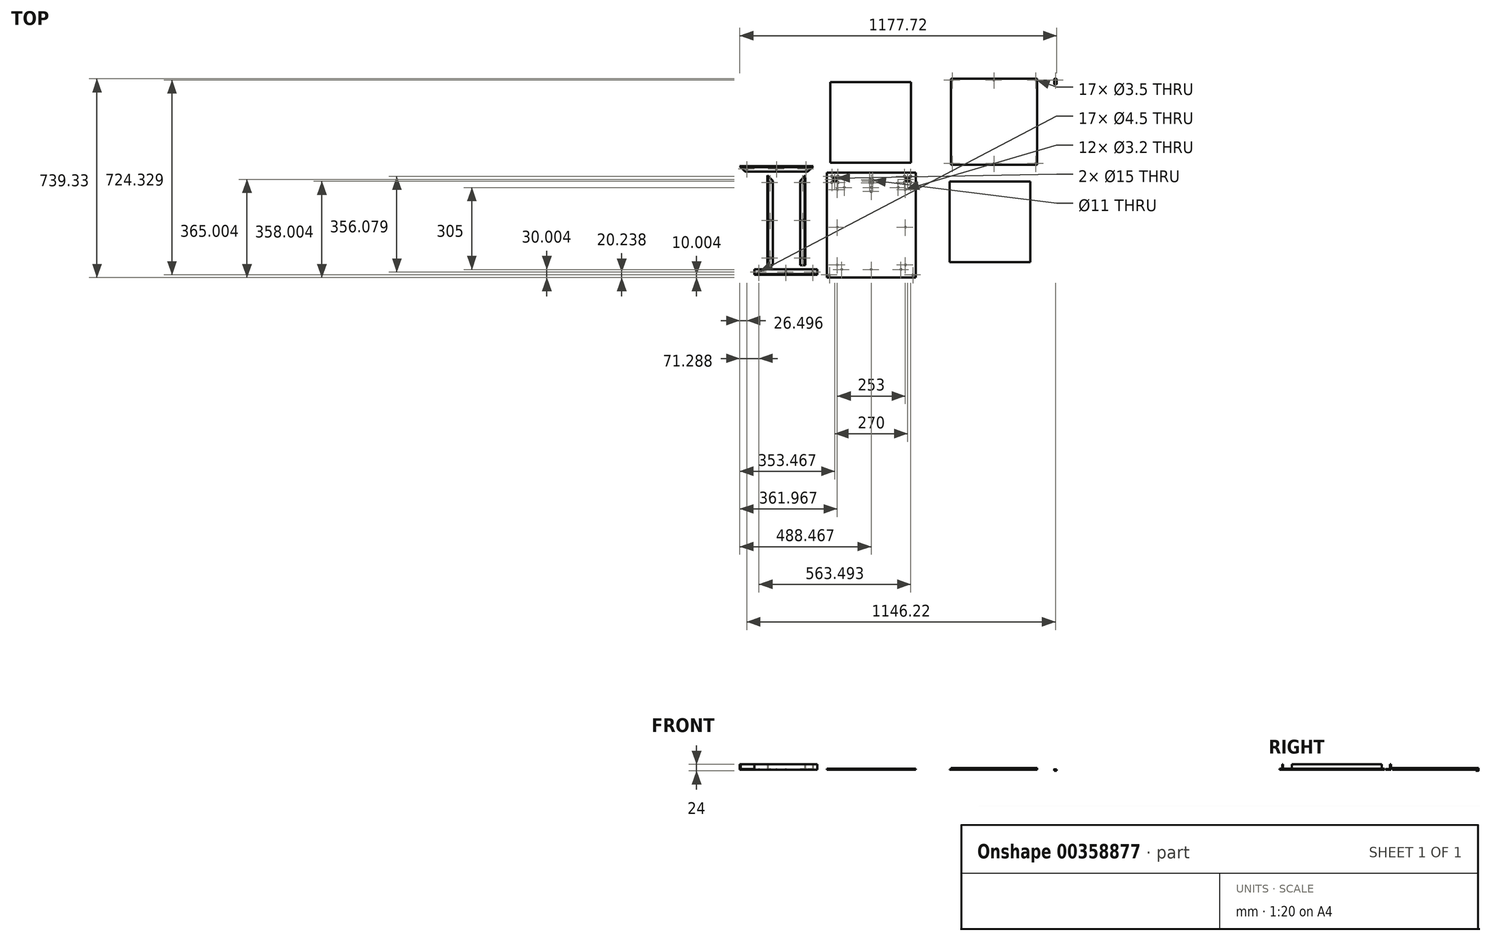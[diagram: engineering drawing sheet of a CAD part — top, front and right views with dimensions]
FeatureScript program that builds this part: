
annotation { "Feature Type Name" : "Feature", "Feature Type Description" : "" }
export const myFeature = defineFeature(function(context is Context, id is Id, definition is map)
    precondition{}
    {
        {
            var Q0;
            Q0=qCreatedBy(makeId("Top.planeOp"),FACE);
            var sketch = newSketch(context, id + "F0", { "sketchPlane" : qUnion([Q0])});
            skLineSegment(sketch, "E0.bottom", {"start": v(150, 187.33) * mm, "end": v(480, 187.33) * mm});
            skLineSegment(sketch, "E0.top", {"start": v(150, -202.67) * mm, "end": v(480, -202.67) * mm});
            skLineSegment(sketch, "E0.left", {"start": v(150, 187.33) * mm, "end": v(150, -202.67) * mm});
            skLineSegment(sketch, "E0.right", {"start": v(480, 187.33) * mm, "end": v(480, -202.67) * mm});
            skCircle(sketch, "E1", {"center": v(180, 162.33) * mm, "radius": 7.5 * mm});
            skCircle(sketch, "E2", {"center": v(450, 162.33) * mm, "radius": 7.5 * mm});
            skCircle(sketch, "E3", {"center": v(315, 155.33) * mm, "radius": 5.5 * mm});
            skPoint(sketch, "E3.centerSnap0", {"position": v(315, 187.33) * mm});
            skLineSegment(sketch, "E4", {"start": v(150, -202.67) * mm, "end": v(480, 187.33) * mm, "construction": true});
            skLineSegment(sketch, "E5.bottom", {"start": v(470, -192.67) * mm, "end": v(160, -192.67) * mm, "construction": true});
            skLineSegment(sketch, "E5.top", {"start": v(470, 117.33) * mm, "end": v(160, 117.33) * mm, "construction": true});
            skLineSegment(sketch, "E5.left", {"start": v(470, -192.67) * mm, "end": v(470, 117.33) * mm, "construction": true});
            skLineSegment(sketch, "E5.right", {"start": v(160, -192.67) * mm, "end": v(160, 117.33) * mm, "construction": true});
            skPoint(sketch, "E5.middle", {"position": v(315, -37.67) * mm});
            skCircle(sketch, "E6", {"center": v(315, 117.33) * mm, "radius": 1.75 * mm});
            skCircle(sketch, "E7", {"center": v(160, -192.67) * mm, "radius": 1.75 * mm});
            skCircle(sketch, "E8", {"center": v(470, -192.67) * mm, "radius": 1.75 * mm});
            skLineSegment(sketch, "E9", {"start": v(315, -7.67) * mm, "end": v(315, -37.67) * mm, "construction": true});
            skLineSegment(sketch, "E10", {"start": v(315, -37.67) * mm, "end": v(315, -37.67) * mm});
            skCircle(sketch, "E11", {"center": v(180, 162.33) * mm, "radius": 16 * mm, "construction": true});
            skCircle(sketch, "E12", {"center": v(168.7, 151.02) * mm, "radius": 2.25 * mm});
            skCircle(sketch, "E13", {"center": v(168.7, 173.65) * mm, "radius": 2.25 * mm});
            skCircle(sketch, "E14", {"center": v(191.32, 173.65) * mm, "radius": 2.25 * mm});
            skCircle(sketch, "E15", {"center": v(191.32, 151.02) * mm, "radius": 2.25 * mm});
            skLineSegment(sketch, "E16.bottom", {"start": v(168.7, 173.65) * mm, "end": v(191.32, 173.65) * mm, "construction": true});
            skLineSegment(sketch, "E16.top", {"start": v(168.7, 151.02) * mm, "end": v(191.32, 151.02) * mm, "construction": true});
            skLineSegment(sketch, "E16.left", {"start": v(168.7, 173.65) * mm, "end": v(168.7, 151.02) * mm, "construction": true});
            skLineSegment(sketch, "E16.right", {"start": v(191.32, 173.65) * mm, "end": v(191.32, 151.02) * mm, "construction": true});
            skCircle(sketch, "E17", {"center": v(450, 162.33) * mm, "radius": 16 * mm, "construction": true});
            skLineSegment(sketch, "E18.bottom", {"start": v(438.7, 173.65) * mm, "end": v(461.32, 173.65) * mm, "construction": true});
            skLineSegment(sketch, "E18.top", {"start": v(438.7, 151.02) * mm, "end": v(461.32, 151.02) * mm, "construction": true});
            skLineSegment(sketch, "E18.left", {"start": v(438.7, 173.65) * mm, "end": v(438.7, 151.02) * mm, "construction": true});
            skLineSegment(sketch, "E18.right", {"start": v(461.32, 173.65) * mm, "end": v(461.32, 151.02) * mm, "construction": true});
            skCircle(sketch, "E19", {"center": v(438.7, 173.65) * mm, "radius": 2.25 * mm});
            skCircle(sketch, "E20", {"center": v(461.32, 173.65) * mm, "radius": 2.25 * mm});
            skCircle(sketch, "E21", {"center": v(461.32, 151.02) * mm, "radius": 2.25 * mm});
            skCircle(sketch, "E22", {"center": v(438.7, 151.02) * mm, "radius": 2.25 * mm});
            skCircle(sketch, "E23", {"center": v(315, 155.33) * mm, "radius": 8 * mm, "construction": true});
            skLineSegment(sketch, "E24.bottom", {"start": v(309.35, 161) * mm, "end": v(320.66, 161) * mm, "construction": true});
            skLineSegment(sketch, "E24.top", {"start": v(309.35, 149.68) * mm, "end": v(320.66, 149.68) * mm, "construction": true});
            skLineSegment(sketch, "E24.left", {"start": v(309.35, 161) * mm, "end": v(309.35, 149.68) * mm, "construction": true});
            skLineSegment(sketch, "E24.right", {"start": v(320.66, 161) * mm, "end": v(320.66, 149.68) * mm, "construction": true});
            skCircle(sketch, "E25", {"center": v(309.35, 161) * mm, "radius": 1.75 * mm});
            skCircle(sketch, "E26", {"center": v(320.66, 161) * mm, "radius": 1.75 * mm});
            skCircle(sketch, "E27", {"center": v(320.66, 149.68) * mm, "radius": 1.75 * mm});
            skCircle(sketch, "E28", {"center": v(309.35, 149.68) * mm, "radius": 1.75 * mm});
            skCircle(sketch, "E29", {"center": v(188.5, -155.42) * mm, "radius": 1.6 * mm});
            skCircle(sketch, "E30", {"center": v(315, -172.67) * mm, "radius": 1.6 * mm});
            skPoint(sketch, "E30.centerSnap0", {"position": v(315, -202.67) * mm});
            skCircle(sketch, "E31", {"center": v(205, -172.67) * mm, "radius": 1.6 * mm});
            skCircle(sketch, "E32", {"center": v(425, -172.67) * mm, "radius": 1.6 * mm});
            skCircle(sketch, "E33", {"center": v(441.5, -155.42) * mm, "radius": 1.6 * mm});
            skCircle(sketch, "E34", {"center": v(188.5, -15.42) * mm, "radius": 1.6 * mm});
            skCircle(sketch, "E35", {"center": v(188.5, 124.58) * mm, "radius": 1.6 * mm});
            skCircle(sketch, "E36", {"center": v(441.5, -15.42) * mm, "radius": 1.6 * mm});
            skCircle(sketch, "E37", {"center": v(441.5, 124.58) * mm, "radius": 1.6 * mm});
            skCircle(sketch, "E38", {"center": v(315, 132.33) * mm, "radius": 1.6 * mm});
            skCircle(sketch, "E39", {"center": v(415, 132.33) * mm, "radius": 1.6 * mm});
            skCircle(sketch, "E40", {"center": v(215, 132.33) * mm, "radius": 1.6 * mm});
            skSolve(sketch);
        }
        {
            var Q0;
            Q0=makeQuery(id+"F0.imprint","IMPRINT",FACE,{"disambiguationData":[TD([[makeQuery(id+"F0.imprint","IMPRINT",EDGE,{"derivedFrom":sQuery(id+"F0.wireOp",EDGE,"E0.bottom")}),-1.0]])]});
            extrude(context, id + "F1", {"entities" : qUnion([Q0]), "depth" : 4 * mm});
        }
        {
            var Q0;
            Q0=qCreatedBy(makeId("Top.planeOp"),FACE);
            var sketch = newSketch(context, id + "F2", { "sketchPlane" : qUnion([Q0])});
            skLineSegment(sketch, "E41.bottom", {"start": v(605.69, 155) * mm, "end": v(905.69, 155) * mm});
            skLineSegment(sketch, "E41.top", {"start": v(605.69, -145) * mm, "end": v(905.69, -145) * mm});
            skLineSegment(sketch, "E41.left", {"start": v(605.69, 155) * mm, "end": v(605.69, -145) * mm});
            skLineSegment(sketch, "E41.right", {"start": v(905.69, 155) * mm, "end": v(905.69, -145) * mm});
            skSolve(sketch);
        }
        {
            var Q0;
            Q0=makeQuery(id+"F2.imprint","IMPRINT",FACE,{"disambiguationData":[TD([[makeQuery(id+"F2.imprint","IMPRINT",EDGE,{"derivedFrom":sQuery(id+"F2.wireOp",EDGE,"E41.bottom")}),-1.0]])]});
            extrude(context, id + "F3", {"entities" : qUnion([Q0]), "depth" : 2 * mm});
        }
        {
            var Q0;
            Q0=qCreatedBy(makeId("Top.planeOp"),FACE);
            var sketch = newSketch(context, id + "F4", { "sketchPlane" : qUnion([Q0])});
            skLineSegment(sketch, "E42.bottom", {"start": v(611.16, 536.66) * mm, "end": v(931.16, 536.66) * mm});
            skLineSegment(sketch, "E42.top", {"start": v(611.16, 216.66) * mm, "end": v(931.16, 216.66) * mm});
            skLineSegment(sketch, "E42.left", {"start": v(611.16, 536.66) * mm, "end": v(611.16, 216.66) * mm});
            skLineSegment(sketch, "E42.right", {"start": v(931.16, 536.66) * mm, "end": v(931.16, 216.66) * mm});
            skCircle(sketch, "E43", {"center": v(771.16, 531.66) * mm, "radius": 1.75 * mm});
            skPoint(sketch, "E43.centerSnap0", {"position": v(771.16, 536.66) * mm});
            skLineSegment(sketch, "E44", {"start": v(611.16, 216.66) * mm, "end": v(931.16, 536.66) * mm, "construction": true});
            skLineSegment(sketch, "E45", {"start": v(611.16, 536.66) * mm, "end": v(931.16, 216.66) * mm, "construction": true});
            skCircle(sketch, "E46", {"center": v(616.16, 221.66) * mm, "radius": 1.75 * mm});
            skCircle(sketch, "E47", {"center": v(926.16, 221.66) * mm, "radius": 1.75 * mm});
            skCircle(sketch, "E48", {"center": v(771.16, 221.66) * mm, "radius": 1.75 * mm});
            skPoint(sketch, "E48.centerSnap0", {"position": v(771.16, 216.66) * mm});
            skCircle(sketch, "E49", {"center": v(616.16, 531.66) * mm, "radius": 1.75 * mm});
            skCircle(sketch, "E50", {"center": v(926.16, 531.66) * mm, "radius": 1.75 * mm});
            skSolve(sketch);
        }
        {
            var Q0;
            Q0=makeQuery(id+"F4.imprint","IMPRINT",FACE,{"disambiguationData":[TD([[makeQuery(id+"F4.imprint","IMPRINT",EDGE,{"derivedFrom":sQuery(id+"F4.wireOp",EDGE,"E42.bottom")}),-1.0]])]});
            extrude(context, id + "F5", {"entities" : qUnion([Q0]), "depth" : 6 * mm});
        }
        {
            var Q0;
            Q0=qCreatedBy(makeId("Top.planeOp"),FACE);
            var sketch = newSketch(context, id + "F6", { "sketchPlane" : qUnion([Q0])});
            skLineSegment(sketch, "E51.bottom", {"start": v(162.3, 524.65) * mm, "end": v(462.3, 524.65) * mm});
            skLineSegment(sketch, "E51.top", {"start": v(162.3, 224.65) * mm, "end": v(462.3, 224.65) * mm});
            skLineSegment(sketch, "E51.left", {"start": v(162.3, 524.65) * mm, "end": v(162.3, 224.65) * mm});
            skLineSegment(sketch, "E51.right", {"start": v(462.3, 524.65) * mm, "end": v(462.3, 224.65) * mm});
            skSolve(sketch);
        }
        {
            var Q0;
            Q0=qSketchRegion(id+"F6",true);
            extrude(context, id + "F7", {"entities" : qUnion([Q0]), "depth" : 4 * mm});
        }
        {
            var Q0;
            Q0=qCreatedBy(makeId("Top.planeOp"),FACE);
            var sketch = newSketch(context, id + "F8", { "sketchPlane" : qUnion([Q0])});
            skCircle(sketch, "E52", {"center": v(999.26, 531.22) * mm, "radius": 1.75 * mm});
            skCircle(sketch, "E53", {"center": v(999.26, 531.22) * mm, "radius": 5 * mm});
            skLineSegment(sketch, "E54.bottom", {"start": v(994.26, 536.22) * mm, "end": v(1004.26, 536.22) * mm});
            skLineSegment(sketch, "E54.top", {"start": v(994.26, 516.22) * mm, "end": v(1004.26, 516.22) * mm});
            skLineSegment(sketch, "E54.left", {"start": v(994.26, 536.22) * mm, "end": v(994.26, 516.22) * mm});
            skLineSegment(sketch, "E54.right", {"start": v(1004.26, 536.22) * mm, "end": v(1004.26, 516.22) * mm});
            skSolve(sketch);
        }
        {
            var Q0;
            Q0=makeQuery(id+"F8.imprint","IMPRINT",FACE,{"disambiguationData":[TD([[makeQuery(id+"F8.imprint","IMPRINT",EDGE,{"derivedFrom":sQuery(id+"F8.wireOp",EDGE,"E52")}),-1.0]])]});
            var Q1;
            {var subQ0=sQuery(id+"F8.wireOp",EDGE,"E54.bottom");var subQ1=sQuery(id+"F8.wireOp",EDGE,"E53");var subQ2=makeQuery(id+"F8.imprint","INTERSECT",VERTEX,{"derivedFrom":[subQ1,subQ0]});Q1=makeQuery(id+"F8.imprint","IMPRINT",FACE,{"disambiguationData":[TD([[makeQuery(id+"F8.imprint","IMPRINT",EDGE,{"disambiguationData":[TD([[subQ2,-1.0]])],"derivedFrom":subQ1}),-1.0]])]});}
            var Q2;
            {var subQ0=sQuery(id+"F8.wireOp",EDGE,"E54.bottom");var subQ1=sQuery(id+"F8.wireOp",EDGE,"E53");var subQ2=makeQuery(id+"F8.imprint","INTERSECT",VERTEX,{"derivedFrom":[subQ1,subQ0]});Q2=makeQuery(id+"F8.imprint","IMPRINT",FACE,{"disambiguationData":[TD([[makeQuery(id+"F8.imprint","IMPRINT",EDGE,{"disambiguationData":[TD([[subQ2,1.0]])],"derivedFrom":subQ1}),-1.0]])]});}
            extrude(context, id + "F9", {"entities" : qUnion([Q0, Q1, Q2]), "oppositeDirection" : true, "depth" : 4 * mm});
        }
        {
            var Q0;
            Q0=qSketchRegion(id+"F8",true);
            extrude(context, id + "F10", {"entities" : qUnion([Q0]), "operationType" : NewBodyOperationType.ADD, "depth" : 2 * mm});
        }
        {
            var Q0;
            Q0=makeQuery(id+"F10.opExtrude","SWEPT_EDGE",EDGE,{"disambiguationData":[OSD([sQuery(id+"F8.wireOp",EDGE,"E54.top"),sQuery(id+"F8.wireOp",EDGE,"E54.left")])]});
            var Q1;
            Q1=makeQuery(id+"F10.opExtrude","SWEPT_EDGE",EDGE,{"disambiguationData":[OSD([sQuery(id+"F8.wireOp",EDGE,"E54.top"),sQuery(id+"F8.wireOp",EDGE,"E54.right")])]});
            var Q2;
            {var subQ0=sQuery(id+"F8.wireOp",EDGE,"E54.right");var subQ1=sQuery(id+"F8.wireOp",EDGE,"E54.bottom");Q2=makeQuery(id+"F10.boolean.opBoolean","MERGE",EDGE,{"derivedFrom":[makeQuery(id+"F9.opExtrude","SWEPT_EDGE",EDGE,{"disambiguationData":[OSD([subQ1,subQ0])]}),makeQuery(id+"F10.opExtrude","SWEPT_EDGE",EDGE,{"disambiguationData":[OSD([subQ1,subQ0])]})]});}
            var Q3;
            {var subQ0=sQuery(id+"F8.wireOp",EDGE,"E54.left");var subQ1=sQuery(id+"F8.wireOp",EDGE,"E54.bottom");Q3=makeQuery(id+"F10.boolean.opBoolean","MERGE",EDGE,{"derivedFrom":[makeQuery(id+"F9.opExtrude","SWEPT_EDGE",EDGE,{"disambiguationData":[OSD([subQ1,subQ0])]}),makeQuery(id+"F10.opExtrude","SWEPT_EDGE",EDGE,{"disambiguationData":[OSD([subQ1,subQ0])]})]});}
            fillet(context, id + "F11", {"entities" : qUnion([Q0, Q1, Q2, Q3]), "radius" : 2 * mm, "tangentPropagation" : true, "allowEdgeOverflow" : false});
        }
        {
            var Q0;
            Q0=qCreatedBy(makeId("Top.planeOp"),FACE);
            var sketch = newSketch(context, id + "F12", { "sketchPlane" : qUnion([Q0])});
            skLineSegment(sketch, "E55.bottom", {"start": v(-70.66, 177.44) * mm, "end": v(-50.66, 177.44) * mm});
            skLineSegment(sketch, "E55.top", {"start": v(-70.66, -157.06) * mm, "end": v(-50.66, -157.06) * mm});
            skLineSegment(sketch, "E55.left", {"start": v(-70.66, 177.44) * mm, "end": v(-70.66, -157.06) * mm});
            skLineSegment(sketch, "E55.right", {"start": v(-50.66, 177.44) * mm, "end": v(-50.66, -157.06) * mm});
            skLineSegment(sketch, "E56", {"start": v(-70.66, 177.44) * mm, "end": v(-50.66, 157.44) * mm});
            skCircle(sketch, "E57", {"center": v(-60.66, -129.8) * mm, "radius": 2.25 * mm});
            skPoint(sketch, "E57.centerSnap0", {"position": v(-60.66, -157.06) * mm});
            skCircle(sketch, "E58", {"center": v(-60.66, 10.2) * mm, "radius": 2.25 * mm});
            skPoint(sketch, "E58.centerSnap0", {"position": v(-50.66, 10.2) * mm});
            skCircle(sketch, "E59", {"center": v(-60.66, 150.2) * mm, "radius": 2.25 * mm});
            skPoint(sketch, "E59.centerSnap0", {"position": v(-60.66, 167.44) * mm});
            skSolve(sketch);
        }
        {
            var Q0;
            {var subQ0=sQuery(id+"F12.wireOp",EDGE,"E55.top");Q0=makeQuery(id+"F12.imprint","IMPRINT",FACE,{"disambiguationData":[TD([[makeQuery(id+"F12.imprint","IMPRINT",EDGE,{"derivedFrom":subQ0}),1.0]])]});}
            extrude(context, id + "F13", {"entities" : qUnion([Q0]), "depth" : 3 * mm});
        }
        {
            var Q0;
            Q0=makeQuery(id+"F13.opExtrude","CAP_FACE",FACE,{"disambiguationData":[OSD([sQuery(id+"F12.wireOp",EDGE,"E55.top"),sQuery(id+"F12.wireOp",EDGE,"E55.left"),sQuery(id+"F12.wireOp",EDGE,"E55.right"),sQuery(id+"F12.wireOp",EDGE,"E56")])],"isStart":true});
            var sketch = newSketch(context, id + "F14", { "sketchPlane" : qUnion([Q0])});
            skLineSegment(sketch, "E60", {"start": v(-70.66, -177.44) * mm, "end": v(-70.66, 157.06) * mm});
            skLineSegment(sketch, "E61", {"start": v(-70.66, 157.06) * mm, "end": v(-67.66, 157.06) * mm});
            skLineSegment(sketch, "E62", {"start": v(-67.66, 157.06) * mm, "end": v(-67.66, -174.44) * mm});
            skLineSegment(sketch, "E63", {"start": v(-67.66, -174.44) * mm, "end": v(-70.66, -177.44) * mm});
            skSolve(sketch);
        }
        {
            var Q0;
            Q0=makeQuery(id+"F14.imprint","IMPRINT",FACE,{"disambiguationData":[TD([[makeQuery(id+"F14.imprint","IMPRINT",EDGE,{"derivedFrom":sQuery(id+"F14.wireOp",EDGE,"E60")}),-1.0]])]});
            extrude(context, id + "F15", {"entities" : qUnion([Q0]), "operationType" : NewBodyOperationType.ADD, "oppositeDirection" : true, "depth" : 20 * mm});
        }
        {
            var Q0;
            Q0=makeQuery(id+"F13.opExtrude","SWEPT_BODY",BODY,{"disambiguationData":[OSD([sQuery(id+"F12.wireOp",EDGE,"E55.top"),sQuery(id+"F12.wireOp",EDGE,"E55.left"),sQuery(id+"F12.wireOp",EDGE,"E55.right"),sQuery(id+"F12.wireOp",EDGE,"E56"),sQuery(id+"F12.wireOp",EDGE,"E57"),sQuery(id+"F12.wireOp",EDGE,"E58"),sQuery(id+"F12.wireOp",EDGE,"E59")])]});
            var Q1;
            Q1=qCreatedBy(makeId("Right.planeOp"),FACE);
            mirror(context, id + "F16", {"entities" : qUnion([Q0]), "mirrorPlane" : qUnion([Q1])});
        }
        {
            var Q0;
            Q0=qCreatedBy(makeId("Top.planeOp"),FACE);
            var sketch = newSketch(context, id + "F17", { "sketchPlane" : qUnion([Q0])});
            skLineSegment(sketch, "E64.bottom", {"start": v(-173.46, 211.15) * mm, "end": v(99.54, 211.15) * mm});
            skLineSegment(sketch, "E64.top", {"start": v(-173.46, 191.15) * mm, "end": v(99.54, 191.15) * mm});
            skLineSegment(sketch, "E64.left", {"start": v(-173.46, 211.15) * mm, "end": v(-173.46, 191.15) * mm});
            skLineSegment(sketch, "E64.right", {"start": v(99.54, 211.15) * mm, "end": v(99.54, 191.15) * mm});
            skLineSegment(sketch, "E65", {"start": v(-173.46, 211.15) * mm, "end": v(-153.46, 191.15) * mm});
            skLineSegment(sketch, "E66", {"start": v(99.54, 211.15) * mm, "end": v(79.54, 191.15) * mm});
            skCircle(sketch, "E67", {"center": v(-146.96, 201.15) * mm, "radius": 1.75 * mm});
            skPoint(sketch, "E67.centerSnap0", {"position": v(-163.46, 201.15) * mm});
            skCircle(sketch, "E68", {"center": v(-36.96, 201.15) * mm, "radius": 1.75 * mm});
            skPoint(sketch, "E68.centerSnap0", {"position": v(-36.96, 191.15) * mm});
            skCircle(sketch, "E69", {"center": v(73.04, 201.15) * mm, "radius": 1.75 * mm});
            skPoint(sketch, "E69.centerSnap0", {"position": v(89.54, 201.15) * mm});
            skSolve(sketch);
        }
        {
            var Q0;
            Q0=makeQuery(id+"F17.imprint","IMPRINT",FACE,{"disambiguationData":[TD([[makeQuery(id+"F17.imprint","IMPRINT",EDGE,{"derivedFrom":sQuery(id+"F17.wireOp",EDGE,"E64.bottom")}),-1.0]])]});
            extrude(context, id + "F18", {"entities" : qUnion([Q0]), "depth" : 3 * mm});
        }
        {
            var Q0;
            Q0=makeQuery(id+"F18.opExtrude","CAP_FACE",FACE,{"disambiguationData":[OSD([sQuery(id+"F17.wireOp",EDGE,"E64.bottom"),sQuery(id+"F17.wireOp",EDGE,"E64.top"),sQuery(id+"F17.wireOp",EDGE,"E65"),sQuery(id+"F17.wireOp",EDGE,"E66")])],"isStart":true});
            var sketch = newSketch(context, id + "F19", { "sketchPlane" : qUnion([Q0])});
            skLineSegment(sketch, "E70", {"start": v(-173.46, -211.15) * mm, "end": v(99.54, -211.15) * mm});
            skLineSegment(sketch, "E71", {"start": v(99.54, -211.15) * mm, "end": v(96.54, -208.15) * mm});
            skLineSegment(sketch, "E72", {"start": v(96.54, -208.15) * mm, "end": v(-170.46, -208.15) * mm});
            skLineSegment(sketch, "E73", {"start": v(-170.46, -208.15) * mm, "end": v(-173.46, -211.15) * mm});
            skSolve(sketch);
        }
        {
            var Q0;
            Q0=qSketchRegion(id+"F19",true);
            extrude(context, id + "F20", {"entities" : qUnion([Q0]), "operationType" : NewBodyOperationType.ADD, "oppositeDirection" : true, "depth" : 20 * mm});
        }
        {
            var Q0;
            Q0=qCreatedBy(makeId("Top.planeOp"),FACE);
            var sketch = newSketch(context, id + "F21", { "sketchPlane" : qUnion([Q0])});
            skLineSegment(sketch, "E74.bottom", {"start": v(-118.67, -172.43) * mm, "end": v(114.33, -172.43) * mm});
            skLineSegment(sketch, "E74.top", {"start": v(-118.67, -192.43) * mm, "end": v(114.33, -192.43) * mm});
            skLineSegment(sketch, "E74.left", {"start": v(-118.67, -172.43) * mm, "end": v(-118.67, -192.43) * mm});
            skLineSegment(sketch, "E74.right", {"start": v(114.33, -172.43) * mm, "end": v(114.33, -192.43) * mm});
            skCircle(sketch, "E75", {"center": v(-102.17, -182.43) * mm, "radius": 2.25 * mm});
            skPoint(sketch, "E75.centerSnap0", {"position": v(-118.67, -182.43) * mm});
            skCircle(sketch, "E76", {"center": v(-2.17, -182.43) * mm, "radius": 2.25 * mm});
            skPoint(sketch, "E76.centerSnap0", {"position": v(-2.17, -172.43) * mm});
            skCircle(sketch, "E77", {"center": v(97.83, -182.43) * mm, "radius": 2.25 * mm});
            skLineSegment(sketch, "E78", {"start": v(-118.67, -189.43) * mm, "end": v(114.33, -189.43) * mm});
            skSolve(sketch);
        }
        {
            var Q0;
            Q0 = qSketchRegion(id + "F21", true);
            extrude(context, id + "F22", {"entities" : qUnion([Q0]), "depth" : 3 * mm});
        }
        {
            var Q0;
            {var subQ0=sQuery(id+"F21.wireOp",EDGE,"E74.top");Q0=makeQuery(id+"F21.imprint","IMPRINT",FACE,{"disambiguationData":[TD([[makeQuery(id+"F21.imprint","IMPRINT",EDGE,{"derivedFrom":subQ0}),1.0]])]});}
            extrude(context, id + "F23", {"entities" : qUnion([Q0]), "operationType" : NewBodyOperationType.ADD, "depth" : 20 * mm});
        }
    });
